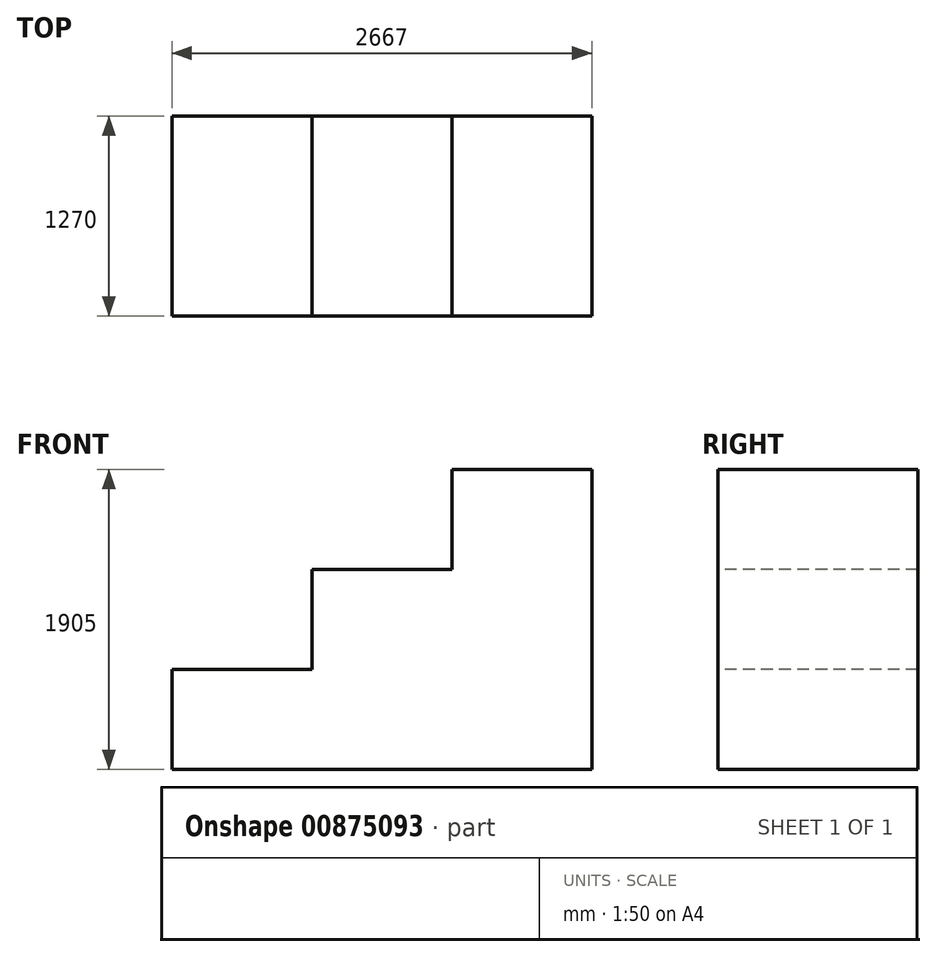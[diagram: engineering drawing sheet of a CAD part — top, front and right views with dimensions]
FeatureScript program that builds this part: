
annotation { "Feature Type Name" : "Feature", "Feature Type Description" : "" }
export const myFeature = defineFeature(function(context is Context, id is Id, definition is map)
    precondition{}
    {
        {
            var Q0;
            Q0=qCreatedBy(makeId("Front.planeOp"),FACE);
            var sketch = newSketch(context, id + "F0", { "sketchPlane" : qUnion([Q0])});
            skLineSegment(sketch, "E0", {"start": v(0, 0) * mm, "end": v(2667, 0) * mm});
            skLineSegment(sketch, "E1", {"start": v(2667, 0) * mm, "end": v(2667, 1905) * mm});
            skLineSegment(sketch, "E2", {"start": v(2667, 1905) * mm, "end": v(0, 1905) * mm});
            skLineSegment(sketch, "E3", {"start": v(0, 1905) * mm, "end": v(0, 0) * mm});
            skSolve(sketch);
        }
        {
            var Q0;
            Q0=makeQuery(id+"F0.imprint","IMPRINT",FACE,{"disambiguationData":[TD([[makeQuery(id+"F0.imprint","IMPRINT",EDGE,{"derivedFrom":sQuery(id+"F0.wireOp",EDGE,"E0")}),1.0]])]});
            extrude(context, id + "F1", {"entities" : qUnion([Q0]), "oppositeDirection" : true, "depth" : 1270 * mm, "offsetDistance" : 25.4 * mm});
        }
        {
            var Q0;
            Q0=makeQuery(id+"F1.opExtrude","CAP_FACE",FACE,{"disambiguationData":[OSD([sQuery(id+"F0.wireOp",EDGE,"E0"),sQuery(id+"F0.wireOp",EDGE,"E1"),sQuery(id+"F0.wireOp",EDGE,"E2"),sQuery(id+"F0.wireOp",EDGE,"E3")])],"isStart":true});
            var sketch = newSketch(context, id + "F2", { "sketchPlane" : qUnion([Q0])});
            skLineSegment(sketch, "E4", {"start": v(2667, 1270) * mm, "end": v(2667, 1905) * mm});
            skLineSegment(sketch, "E5", {"start": v(2667, 1905) * mm, "end": v(0, 1905) * mm});
            skLineSegment(sketch, "E6", {"start": v(0, 1905) * mm, "end": v(0, 0) * mm});
            skLineSegment(sketch, "E7", {"start": v(0, 0) * mm, "end": v(0, 635) * mm});
            skLineSegment(sketch, "E8", {"start": v(0, 635) * mm, "end": v(889, 635) * mm});
            skLineSegment(sketch, "E9", {"start": v(889, 635) * mm, "end": v(889, 1270) * mm});
            skLineSegment(sketch, "E10", {"start": v(889, 1270) * mm, "end": v(1778, 1270) * mm});
            skLineSegment(sketch, "E11", {"start": v(1778, 1270) * mm, "end": v(1778, 1905) * mm});
            skLineSegment(sketch, "E12", {"start": v(1778, 1905) * mm, "end": v(2667, 1905) * mm});
            skLineSegment(sketch, "E13", {"start": v(2667, 1905) * mm, "end": v(2667, 0) * mm});
            skLineSegment(sketch, "E14", {"start": v(2667, 0) * mm, "end": v(0, 0) * mm});
            skLineSegment(sketch, "E15", {"start": v(0, 635) * mm, "end": v(0, 1905) * mm});
            skLineSegment(sketch, "E16", {"start": v(1778, 1905) * mm, "end": v(0, 1905) * mm});
            skSolve(sketch);
        }
        {
            var Q0;
            Q0=makeQuery(id+"F2.imprint","IMPRINT",FACE,{"disambiguationData":[TD([[makeQuery(id+"F2.imprint","IMPRINT",EDGE,{"derivedFrom":sQuery(id+"F2.wireOp",EDGE,"E8")}),1.0]])]});
            extrude(context, id + "F3", {"entities" : qUnion([Q0]), "operationType" : NewBodyOperationType.REMOVE, "oppositeDirection" : true, "depth" : 1270 * mm, "offsetDistance" : 25.4 * mm});
        }
    });
